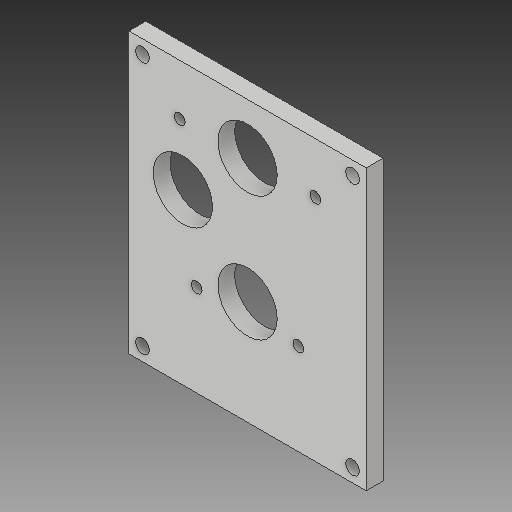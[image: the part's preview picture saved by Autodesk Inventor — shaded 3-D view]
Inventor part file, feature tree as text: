
AUTODESK INVENTOR PART (.ipt)
format: ipt  version: 2018 (Build 220112000, 112)  size: 150,016 bytes
history: native  units: in
note: dims shown in document units (in); Inventor stores cm internally (conversion verified against a paired STEP export)
features: extrude x3, sketch x3
ambient origin geometry x8: Origin, YZ Plane, XZ Plane, XY Plane, X Axis, Y Axis, Z Axis, Center Point
bodies: Solid1 (feature_tree)
feature tree (6):
  extrude  "Extrusion1"  Depth=1.35in
  extrude  "Extrusion2"  Depth=0.875in
  extrude  "Extrusion3"  Depth=0.25in
  sketch  "Sketch1"  dims[d0=0.875in d1=1.35in]
  sketch  "Sketch2"  dims[d2=135.0deg d3=0.875in]
  sketch  "Sketch3"  dims[d7=0.882in d8=0.875in d9=1.0in d10=2.0in d11=0.16in d12=0.75in d13=4.125in d14=1.75in d15=0.25in d16=0.0in d17=1.75in d18=0.2in d19=0.2in d20=0.2031in d21=1.0in d22=0.0in d23=0.75in d24=0.188in d25=0.159in d26=1.0in d27=0.0in]
